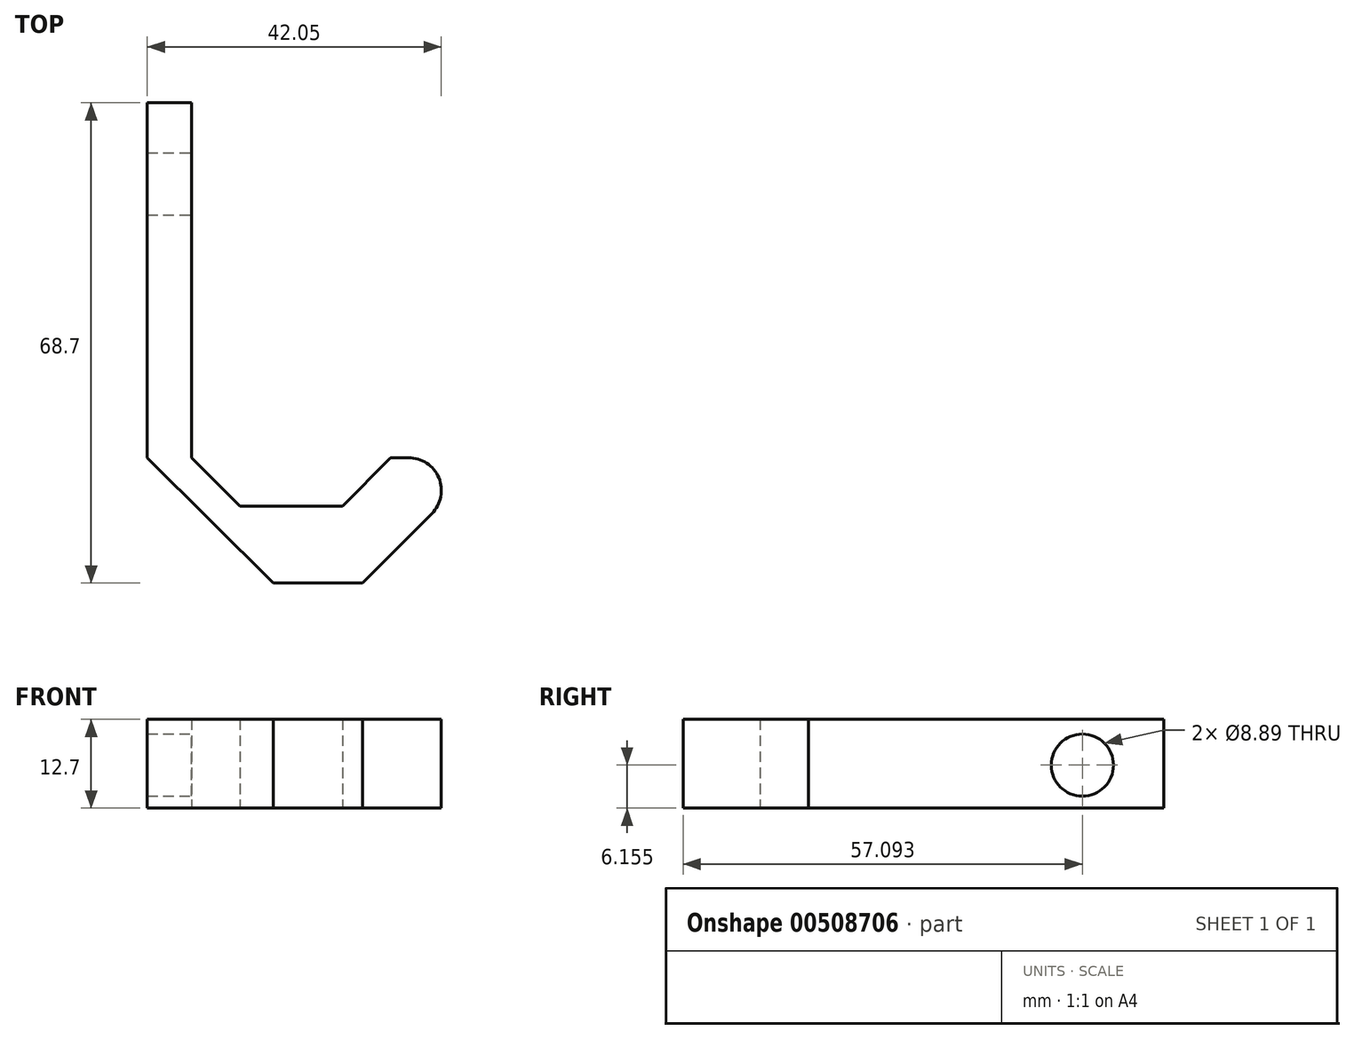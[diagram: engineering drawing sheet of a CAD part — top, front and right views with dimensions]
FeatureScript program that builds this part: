
annotation { "Feature Type Name" : "Feature", "Feature Type Description" : "" }
export const myFeature = defineFeature(function(context is Context, id is Id, definition is map)
    precondition{}
    {
        {
            var Q0;
            Q0=qCreatedBy(makeId("Top.planeOp"),FACE);
            var sketch = newSketch(context, id + "F0", { "sketchPlane" : qUnion([Q0])});
            skLineSegment(sketch, "E0", {"start": v(-71.3, 50.8) * mm, "end": v(-71.3, 0) * mm});
            skLineSegment(sketch, "E1", {"start": v(-71.3, 0) * mm, "end": v(-53.28, -17.9) * mm});
            skLineSegment(sketch, "E2", {"start": v(-53.28, -17.9) * mm, "end": v(-40.5, -17.9) * mm});
            skLineSegment(sketch, "E3", {"start": v(-40.5, -17.9) * mm, "end": v(-22.6, 0.12) * mm});
            skLineSegment(sketch, "E4", {"start": v(-71.3, 50.8) * mm, "end": v(-64.95, 50.8) * mm});
            skLineSegment(sketch, "E5", {"start": v(-64.95, 50.8) * mm, "end": v(-64.95, 0) * mm});
            skLineSegment(sketch, "E6", {"start": v(-64.95, 0) * mm, "end": v(-58.02, -6.89) * mm});
            skLineSegment(sketch, "E7", {"start": v(-58.02, -6.89) * mm, "end": v(-43.36, -6.89) * mm});
            skLineSegment(sketch, "E8", {"start": v(-43.36, -6.89) * mm, "end": v(-36.52, 0) * mm});
            skLineSegment(sketch, "E9", {"start": v(-22.6, 0.12) * mm, "end": v(-36.52, 0) * mm});
            skSolve(sketch);
        }
        {
            var Q0;
            Q0=makeQuery(id+"F0.imprint","IMPRINT",FACE,{"disambiguationData":[TD([[makeQuery(id+"F0.imprint","IMPRINT",EDGE,{"derivedFrom":sQuery(id+"F0.wireOp",EDGE,"E0")}),1.0]])]});
            extrude(context, id + "F1", {"entities" : qUnion([Q0]), "depth" : 12.7 * mm});
        }
        {
            var Q0;
            Q0=makeQuery(id+"F1.opExtrude","SWEPT_EDGE",EDGE,{"disambiguationData":[OSD([sQuery(id+"F0.wireOp",EDGE,"E3"),sQuery(id+"F0.wireOp",EDGE,"E9")])]});
            fillet(context, id + "F2", {"entities" : qUnion([Q0]), "radius" : 4.68 * mm, "tangentPropagation" : true, "allowEdgeOverflow" : false});
        }
        {
            var Q0;
            {var subQ0=sQuery(id+"F0.wireOp",EDGE,"E9");Q0=makeQuery(id+"F2.opFillet","BLEND_EDGE",EDGE,{"blendedFrom":[makeQuery(id+"F1.opExtrude","SWEPT_EDGE",EDGE,{"disambiguationData":[OSD([sQuery(id+"F0.wireOp",EDGE,"E3"),subQ0])]}),makeQuery(id+"F1.opExtrude","SWEPT_FACE",FACE,{"disambiguationData":[OSD([subQ0])]})],"blendedInto":[makeQuery(id+"F1.opExtrude","SWEPT_FACE",FACE,{"disambiguationData":[OSD([subQ0])]})]});}
            var Q1;
            Q1=makeQuery(id+"F1.opExtrude","SWEPT_EDGE",EDGE,{"disambiguationData":[OSD([sQuery(id+"F0.wireOp",EDGE,"E8"),sQuery(id+"F0.wireOp",EDGE,"E9")])]});
            fillet(context, id + "F3", {"entities" : qUnion([Q0, Q1]), "radius" : 0.12 * mm, "tangentPropagation" : true, "allowEdgeOverflow" : false});
        }
        {
            var Q0;
            Q0=qCreatedBy(makeId("Right.planeOp"),FACE);
            var sketch = newSketch(context, id + "F4", { "sketchPlane" : qUnion([Q0])});
            skPoint(sketch, "E10", {"position": v(39.2, 6.16) * mm});
            skSolve(sketch);
        }
        {
            var Q0;
            Q0=sQuery(id+"F4.wireOp",VERTEX,"E10");
            var Q1;
            Q1=makeQuery(id+"F1.opExtrude","SWEPT_BODY",BODY,{"disambiguationData":[OSD([sQuery(id+"F0.wireOp",EDGE,"E0"),sQuery(id+"F0.wireOp",EDGE,"E1"),sQuery(id+"F0.wireOp",EDGE,"E2"),sQuery(id+"F0.wireOp",EDGE,"E3"),sQuery(id+"F0.wireOp",EDGE,"E4"),sQuery(id+"F0.wireOp",EDGE,"E5"),sQuery(id+"F0.wireOp",EDGE,"E6"),sQuery(id+"F0.wireOp",EDGE,"E7"),sQuery(id+"F0.wireOp",EDGE,"E8"),sQuery(id+"F0.wireOp",EDGE,"E9")])]});
            hole(context, id + "F5", {"style" : HoleStyle.SIMPLE, "endStyle" : HoleEndStyle.THROUGH, "holeDiameter" : 8.9 * mm, "isTappedThrough" : true, "tappedDepth" : 12.7 * mm, "tapClearance" : 3, "locations" : qUnion([Q0]), "scope" : qUnion([Q1])});
        }
    });
